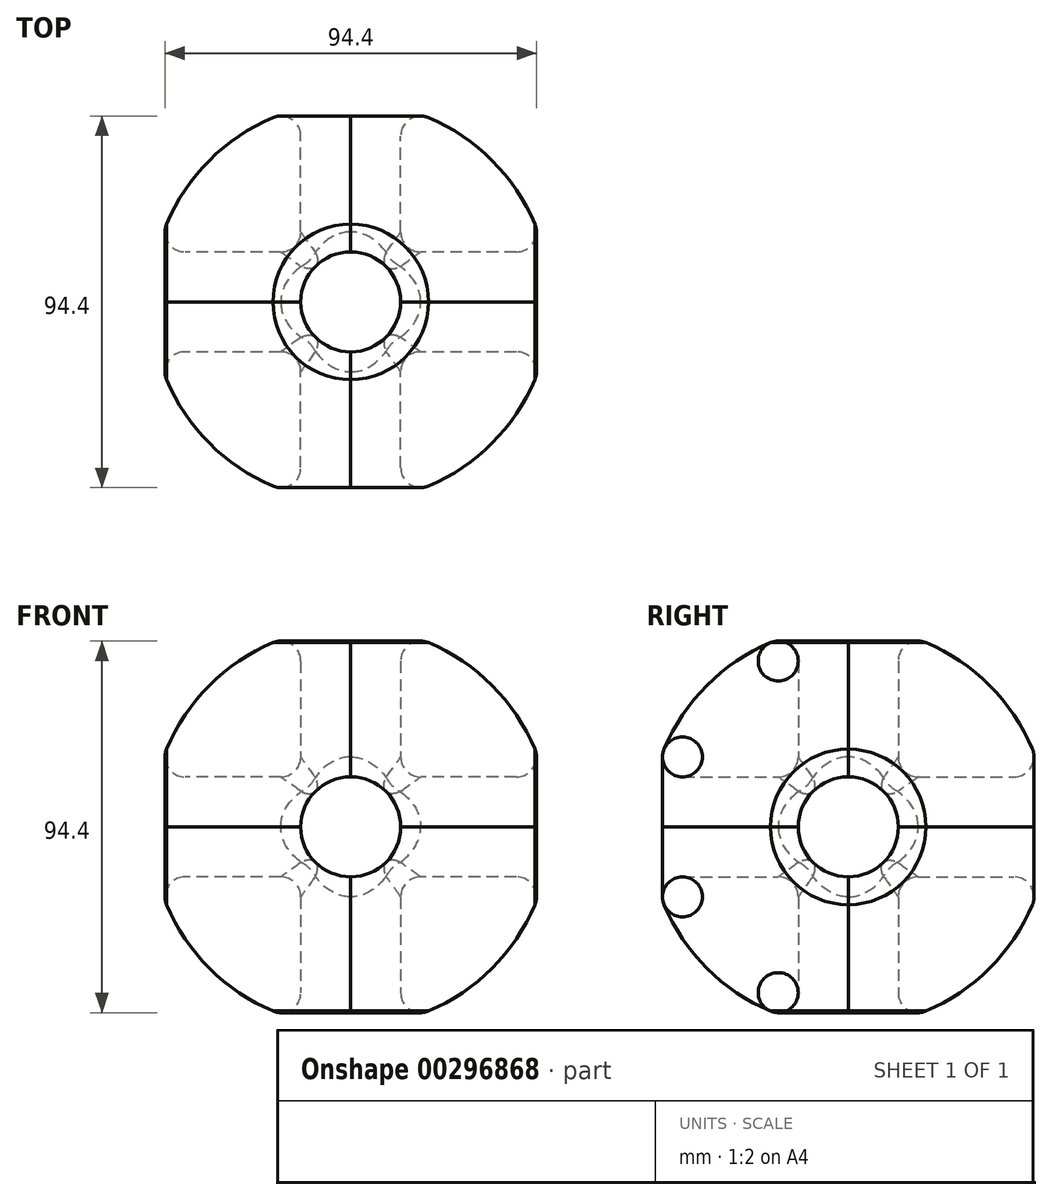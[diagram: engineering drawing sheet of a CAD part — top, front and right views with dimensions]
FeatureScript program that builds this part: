
annotation { "Feature Type Name" : "Feature", "Feature Type Description" : "" }
export const myFeature = defineFeature(function(context is Context, id is Id, definition is map)
    precondition{}
    {
        {
            var Q0;
            Q0=qCreatedBy(makeId("Top.planeOp"),FACE);
            var sketch = newSketch(context, id + "F0", { "sketchPlane" : qUnion([Q0])});
            skCircle(sketch, "E0", {"center": v(0, 0) * mm, "radius": 50.8 * mm});
            skLineSegment(sketch, "E1", {"start": v(0, 50.8) * mm, "end": v(0, -50.8) * mm});
            skLineSegment(sketch, "E2", {"start": v(-50.8, 0) * mm, "end": v(50.8, 0) * mm});
            skSolve(sketch);
        }
        {
            var Q0;
            Q0=qCreatedBy(makeId("Top.planeOp"),FACE);
            var sketch = newSketch(context, id + "F1", { "sketchPlane" : qUnion([Q0])});
            skCircle(sketch, "E3", {"center": v(0, 0) * mm, "radius": 12.7 * mm});
            skSolve(sketch);
        }
        {
            var Q0;
            Q0=qCreatedBy(makeId("Right.planeOp"),FACE);
            var sketch = newSketch(context, id + "F2", { "sketchPlane" : qUnion([Q0])});
            skCircle(sketch, "E4", {"center": v(0, 0) * mm, "radius": 12.7 * mm});
            skSolve(sketch);
        }
        {
            var Q0;
            Q0=qCreatedBy(makeId("Front.planeOp"),FACE);
            var sketch = newSketch(context, id + "F3", { "sketchPlane" : qUnion([Q0])});
            skCircle(sketch, "E5", {"center": v(0, 0) * mm, "radius": 12.7 * mm});
            skSolve(sketch);
        }
        {
            var Q0;
            {var subQ0=sQuery(id+"F0.wireOp",EDGE,"E1");var subQ1=sQuery(id+"F0.wireOp",EDGE,"E0");var subQ2=makeQuery(id+"F0.imprint","INTERSECT",VERTEX,{"disambiguationData":[OD(0.0)],"derivedFrom":[subQ1,subQ0]});Q0=makeQuery(id+"F0.imprint","IMPRINT",FACE,{"disambiguationData":[TD([[makeQuery(id+"F0.imprint","IMPRINT",EDGE,{"disambiguationData":[TD([[subQ2,-1.0]])],"derivedFrom":subQ1}),1.0]])]});}
            var Q1;
            Q1=sQuery(id+"F0.wireOp",EDGE,"E1");
            revolve(context, id + "F4", {"entities" : qUnion([Q0]), "axis" : qUnion([Q1]), "revolveType" : RevolveType.ONE_DIRECTION, "oppositeDirection" : true, "angle" : 90 * degree});
        }
        {
            var Q0;
            {var subQ0=sQuery(id+"F0.wireOp",EDGE,"E1");var subQ1=sQuery(id+"F0.wireOp",EDGE,"E0");var subQ2=makeQuery(id+"F0.imprint","INTERSECT",VERTEX,{"disambiguationData":[OD(0.0)],"derivedFrom":[subQ1,subQ0]});Q0=makeQuery(id+"F0.imprint","IMPRINT",FACE,{"disambiguationData":[TD([[makeQuery(id+"F0.imprint","IMPRINT",EDGE,{"disambiguationData":[TD([[subQ2,1.0]])],"derivedFrom":subQ1}),1.0]])]});}
            var Q1;
            Q1=sQuery(id+"F0.wireOp",EDGE,"E1");
            revolve(context, id + "F5", {"entities" : qUnion([Q0]), "axis" : qUnion([Q1]), "revolveType" : RevolveType.ONE_DIRECTION, "angle" : 90 * degree});
        }
        {
            var Q0;
            {var subQ0=sQuery(id+"F0.wireOp",EDGE,"E1");var subQ1=sQuery(id+"F0.wireOp",EDGE,"E0");var subQ2=makeQuery(id+"F0.imprint","INTERSECT",VERTEX,{"disambiguationData":[OD(1.0)],"derivedFrom":[subQ1,subQ0]});Q0=makeQuery(id+"F0.imprint","IMPRINT",FACE,{"disambiguationData":[TD([[makeQuery(id+"F0.imprint","IMPRINT",EDGE,{"disambiguationData":[TD([[subQ2,1.0]])],"derivedFrom":subQ1}),1.0]])]});}
            var Q1;
            Q1=sQuery(id+"F0.wireOp",EDGE,"E1");
            revolve(context, id + "F6", {"entities" : qUnion([Q0]), "axis" : qUnion([Q1]), "revolveType" : RevolveType.ONE_DIRECTION, "oppositeDirection" : true, "angle" : 90 * degree});
        }
        {
            var Q0;
            {var subQ0=sQuery(id+"F0.wireOp",EDGE,"E1");var subQ1=sQuery(id+"F0.wireOp",EDGE,"E0");var subQ2=makeQuery(id+"F0.imprint","INTERSECT",VERTEX,{"disambiguationData":[OD(1.0)],"derivedFrom":[subQ1,subQ0]});Q0=makeQuery(id+"F0.imprint","IMPRINT",FACE,{"disambiguationData":[TD([[makeQuery(id+"F0.imprint","IMPRINT",EDGE,{"disambiguationData":[TD([[subQ2,-1.0]])],"derivedFrom":subQ1}),1.0]])]});}
            var Q1;
            Q1=sQuery(id+"F0.wireOp",EDGE,"E1");
            revolve(context, id + "F7", {"entities" : qUnion([Q0]), "axis" : qUnion([Q1]), "revolveType" : RevolveType.ONE_DIRECTION, "angle" : 90 * degree});
        }
        {
            var Q0;
            {var subQ0=sQuery(id+"F0.wireOp",EDGE,"E1");var subQ1=sQuery(id+"F0.wireOp",EDGE,"E0");var subQ2=makeQuery(id+"F0.imprint","INTERSECT",VERTEX,{"disambiguationData":[OD(1.0)],"derivedFrom":[subQ1,subQ0]});Q0=makeQuery(id+"F0.imprint","IMPRINT",FACE,{"disambiguationData":[TD([[makeQuery(id+"F0.imprint","IMPRINT",EDGE,{"disambiguationData":[TD([[subQ2,1.0]])],"derivedFrom":subQ1}),1.0]])]});}
            var Q1;
            Q1=sQuery(id+"F0.wireOp",EDGE,"E1");
            revolve(context, id + "F8", {"entities" : qUnion([Q0]), "axis" : qUnion([Q1]), "revolveType" : RevolveType.ONE_DIRECTION, "angle" : 90 * degree});
        }
        {
            var Q0;
            {var subQ0=sQuery(id+"F0.wireOp",EDGE,"E1");var subQ1=sQuery(id+"F0.wireOp",EDGE,"E0");var subQ2=makeQuery(id+"F0.imprint","INTERSECT",VERTEX,{"disambiguationData":[OD(1.0)],"derivedFrom":[subQ1,subQ0]});Q0=makeQuery(id+"F0.imprint","IMPRINT",FACE,{"disambiguationData":[TD([[makeQuery(id+"F0.imprint","IMPRINT",EDGE,{"disambiguationData":[TD([[subQ2,-1.0]])],"derivedFrom":subQ1}),1.0]])]});}
            var Q1;
            Q1=sQuery(id+"F0.wireOp",EDGE,"E1");
            revolve(context, id + "F9", {"entities" : qUnion([Q0]), "axis" : qUnion([Q1]), "revolveType" : RevolveType.ONE_DIRECTION, "oppositeDirection" : true, "angle" : 90 * degree});
        }
        {
            var Q0;
            {var subQ0=sQuery(id+"F0.wireOp",EDGE,"E1");var subQ1=sQuery(id+"F0.wireOp",EDGE,"E0");var subQ2=makeQuery(id+"F0.imprint","INTERSECT",VERTEX,{"disambiguationData":[OD(0.0)],"derivedFrom":[subQ1,subQ0]});Q0=makeQuery(id+"F0.imprint","IMPRINT",FACE,{"disambiguationData":[TD([[makeQuery(id+"F0.imprint","IMPRINT",EDGE,{"disambiguationData":[TD([[subQ2,-1.0]])],"derivedFrom":subQ1}),1.0]])]});}
            var Q1;
            Q1=sQuery(id+"F0.wireOp",EDGE,"E1");
            revolve(context, id + "F10", {"entities" : qUnion([Q0]), "axis" : qUnion([Q1]), "revolveType" : RevolveType.ONE_DIRECTION, "angle" : 90 * degree});
        }
        {
            var Q0;
            {var subQ0=sQuery(id+"F0.wireOp",EDGE,"E1");var subQ1=sQuery(id+"F0.wireOp",EDGE,"E0");var subQ2=makeQuery(id+"F0.imprint","INTERSECT",VERTEX,{"disambiguationData":[OD(0.0)],"derivedFrom":[subQ1,subQ0]});Q0=makeQuery(id+"F0.imprint","IMPRINT",FACE,{"disambiguationData":[TD([[makeQuery(id+"F0.imprint","IMPRINT",EDGE,{"disambiguationData":[TD([[subQ2,1.0]])],"derivedFrom":subQ1}),1.0]])]});}
            var Q1;
            Q1=sQuery(id+"F0.wireOp",EDGE,"E1");
            revolve(context, id + "F11", {"entities" : qUnion([Q0]), "axis" : qUnion([Q1]), "revolveType" : RevolveType.ONE_DIRECTION, "oppositeDirection" : true, "angle" : 90 * degree});
        }
        {
            var Q0;
            Q0 = qSketchRegion(id + "F1", true);
            extrude(context, id + "F12", {"entities" : qUnion([Q0]), "operationType" : NewBodyOperationType.REMOVE, "endBound" : BoundingType.SYMMETRIC, "depth" : 101.6 * mm});
        }
        {
            var Q0;
            Q0 = qSketchRegion(id + "F2", true);
            extrude(context, id + "F13", {"entities" : qUnion([Q0]), "operationType" : NewBodyOperationType.REMOVE, "endBound" : BoundingType.SYMMETRIC, "depth" : 101.6 * mm});
        }
        {
            var Q0;
            Q0 = qSketchRegion(id + "F3", true);
            extrude(context, id + "F14", {"entities" : qUnion([Q0]), "operationType" : NewBodyOperationType.REMOVE, "endBound" : BoundingType.SYMMETRIC, "depth" : 101.6 * mm});
        }
        {
            var Q0;
            Q0=makeQuery(id+"F13.boolean.opBoolean","INTERSECT",EDGE,{"derivedFrom":[makeQuery(id+"F5.opRevolve","SWEPT_FACE",FACE,{"disambiguationData":[OSD([sQuery(id+"F0.wireOp",EDGE,"E0")])]}),makeQuery(id+"F13.opExtrude","SWEPT_FACE",FACE,{"disambiguationData":[OSD([sQuery(id+"F2.wireOp",EDGE,"E4")])]})]});
            var Q1;
            Q1=makeQuery(id+"F13.boolean.opBoolean","INTERSECT",EDGE,{"derivedFrom":[makeQuery(id+"F7.opRevolve","SWEPT_FACE",FACE,{"disambiguationData":[OSD([sQuery(id+"F0.wireOp",EDGE,"E0")])]}),makeQuery(id+"F13.opExtrude","SWEPT_FACE",FACE,{"disambiguationData":[OSD([sQuery(id+"F2.wireOp",EDGE,"E4")])]})]});
            var Q2;
            Q2=makeQuery(id+"F13.boolean.opBoolean","INTERSECT",EDGE,{"derivedFrom":[makeQuery(id+"F9.opRevolve","SWEPT_FACE",FACE,{"disambiguationData":[OSD([sQuery(id+"F0.wireOp",EDGE,"E0")])]}),makeQuery(id+"F13.opExtrude","SWEPT_FACE",FACE,{"disambiguationData":[OSD([sQuery(id+"F2.wireOp",EDGE,"E4")])]})]});
            var Q3;
            Q3=makeQuery(id+"F13.boolean.opBoolean","INTERSECT",EDGE,{"derivedFrom":[makeQuery(id+"F11.opRevolve","SWEPT_FACE",FACE,{"disambiguationData":[OSD([sQuery(id+"F0.wireOp",EDGE,"E0")])]}),makeQuery(id+"F13.opExtrude","SWEPT_FACE",FACE,{"disambiguationData":[OSD([sQuery(id+"F2.wireOp",EDGE,"E4")])]})]});
            var Q4;
            Q4=makeQuery(id+"F12.boolean.opBoolean","INTERSECT",EDGE,{"derivedFrom":[makeQuery(id+"F7.opRevolve","SWEPT_FACE",FACE,{"disambiguationData":[OSD([sQuery(id+"F0.wireOp",EDGE,"E0")])]}),makeQuery(id+"F12.opExtrude","SWEPT_FACE",FACE,{"disambiguationData":[OSD([sQuery(id+"F1.wireOp",EDGE,"E3")])]})]});
            var Q5;
            Q5=makeQuery(id+"F12.boolean.opBoolean","INTERSECT",EDGE,{"derivedFrom":[makeQuery(id+"F5.opRevolve","SWEPT_FACE",FACE,{"disambiguationData":[OSD([sQuery(id+"F0.wireOp",EDGE,"E0")])]}),makeQuery(id+"F12.opExtrude","SWEPT_FACE",FACE,{"disambiguationData":[OSD([sQuery(id+"F1.wireOp",EDGE,"E3")])]})]});
            var Q6;
            Q6=makeQuery(id+"F12.boolean.opBoolean","INTERSECT",EDGE,{"derivedFrom":[makeQuery(id+"F6.opRevolve","SWEPT_FACE",FACE,{"disambiguationData":[OSD([sQuery(id+"F0.wireOp",EDGE,"E0")])]}),makeQuery(id+"F12.opExtrude","SWEPT_FACE",FACE,{"disambiguationData":[OSD([sQuery(id+"F1.wireOp",EDGE,"E3")])]})]});
            var Q7;
            Q7=makeQuery(id+"F12.boolean.opBoolean","INTERSECT",EDGE,{"derivedFrom":[makeQuery(id+"F4.opRevolve","SWEPT_FACE",FACE,{"disambiguationData":[OSD([sQuery(id+"F0.wireOp",EDGE,"E0")])]}),makeQuery(id+"F12.opExtrude","SWEPT_FACE",FACE,{"disambiguationData":[OSD([sQuery(id+"F1.wireOp",EDGE,"E3")])]})]});
            var Q8;
            Q8=makeQuery(id+"F14.boolean.opBoolean","INTERSECT",EDGE,{"derivedFrom":[makeQuery(id+"F5.opRevolve","SWEPT_FACE",FACE,{"disambiguationData":[OSD([sQuery(id+"F0.wireOp",EDGE,"E0")])]}),makeQuery(id+"F14.opExtrude","SWEPT_FACE",FACE,{"disambiguationData":[OSD([sQuery(id+"F3.wireOp",EDGE,"E5")])]})]});
            var Q9;
            Q9=makeQuery(id+"F14.boolean.opBoolean","INTERSECT",EDGE,{"derivedFrom":[makeQuery(id+"F11.opRevolve","SWEPT_FACE",FACE,{"disambiguationData":[OSD([sQuery(id+"F0.wireOp",EDGE,"E0")])]}),makeQuery(id+"F14.opExtrude","SWEPT_FACE",FACE,{"disambiguationData":[OSD([sQuery(id+"F3.wireOp",EDGE,"E5")])]})]});
            var Q10;
            Q10=makeQuery(id+"F14.boolean.opBoolean","INTERSECT",EDGE,{"derivedFrom":[makeQuery(id+"F4.opRevolve","SWEPT_FACE",FACE,{"disambiguationData":[OSD([sQuery(id+"F0.wireOp",EDGE,"E0")])]}),makeQuery(id+"F14.opExtrude","SWEPT_FACE",FACE,{"disambiguationData":[OSD([sQuery(id+"F3.wireOp",EDGE,"E5")])]})]});
            var Q11;
            Q11=makeQuery(id+"F14.boolean.opBoolean","INTERSECT",EDGE,{"derivedFrom":[makeQuery(id+"F10.opRevolve","SWEPT_FACE",FACE,{"disambiguationData":[OSD([sQuery(id+"F0.wireOp",EDGE,"E0")])]}),makeQuery(id+"F14.opExtrude","SWEPT_FACE",FACE,{"disambiguationData":[OSD([sQuery(id+"F3.wireOp",EDGE,"E5")])]})]});
            var Q12;
            Q12=makeQuery(id+"F13.boolean.opBoolean","INTERSECT",EDGE,{"derivedFrom":[makeQuery(id+"F6.opRevolve","SWEPT_FACE",FACE,{"disambiguationData":[OSD([sQuery(id+"F0.wireOp",EDGE,"E0")])]}),makeQuery(id+"F13.opExtrude","SWEPT_FACE",FACE,{"disambiguationData":[OSD([sQuery(id+"F2.wireOp",EDGE,"E4")])]})]});
            var Q13;
            Q13=makeQuery(id+"F13.boolean.opBoolean","INTERSECT",EDGE,{"derivedFrom":[makeQuery(id+"F4.opRevolve","SWEPT_FACE",FACE,{"disambiguationData":[OSD([sQuery(id+"F0.wireOp",EDGE,"E0")])]}),makeQuery(id+"F13.opExtrude","SWEPT_FACE",FACE,{"disambiguationData":[OSD([sQuery(id+"F2.wireOp",EDGE,"E4")])]})]});
            var Q14;
            Q14=makeQuery(id+"F13.boolean.opBoolean","INTERSECT",EDGE,{"derivedFrom":[makeQuery(id+"F8.opRevolve","SWEPT_FACE",FACE,{"disambiguationData":[OSD([sQuery(id+"F0.wireOp",EDGE,"E0")])]}),makeQuery(id+"F13.opExtrude","SWEPT_FACE",FACE,{"disambiguationData":[OSD([sQuery(id+"F2.wireOp",EDGE,"E4")])]})]});
            var Q15;
            Q15=makeQuery(id+"F13.boolean.opBoolean","INTERSECT",EDGE,{"derivedFrom":[makeQuery(id+"F10.opRevolve","SWEPT_FACE",FACE,{"disambiguationData":[OSD([sQuery(id+"F0.wireOp",EDGE,"E0")])]}),makeQuery(id+"F13.opExtrude","SWEPT_FACE",FACE,{"disambiguationData":[OSD([sQuery(id+"F2.wireOp",EDGE,"E4")])]})]});
            var Q16;
            Q16=makeQuery(id+"F14.boolean.opBoolean","INTERSECT",EDGE,{"derivedFrom":[makeQuery(id+"F6.opRevolve","SWEPT_FACE",FACE,{"disambiguationData":[OSD([sQuery(id+"F0.wireOp",EDGE,"E0")])]}),makeQuery(id+"F14.opExtrude","SWEPT_FACE",FACE,{"disambiguationData":[OSD([sQuery(id+"F3.wireOp",EDGE,"E5")])]})]});
            var Q17;
            Q17=makeQuery(id+"F14.boolean.opBoolean","INTERSECT",EDGE,{"derivedFrom":[makeQuery(id+"F8.opRevolve","SWEPT_FACE",FACE,{"disambiguationData":[OSD([sQuery(id+"F0.wireOp",EDGE,"E0")])]}),makeQuery(id+"F14.opExtrude","SWEPT_FACE",FACE,{"disambiguationData":[OSD([sQuery(id+"F3.wireOp",EDGE,"E5")])]})]});
            var Q18;
            Q18=makeQuery(id+"F14.boolean.opBoolean","INTERSECT",EDGE,{"derivedFrom":[makeQuery(id+"F7.opRevolve","SWEPT_FACE",FACE,{"disambiguationData":[OSD([sQuery(id+"F0.wireOp",EDGE,"E0")])]}),makeQuery(id+"F14.opExtrude","SWEPT_FACE",FACE,{"disambiguationData":[OSD([sQuery(id+"F3.wireOp",EDGE,"E5")])]})]});
            var Q19;
            Q19=makeQuery(id+"F14.boolean.opBoolean","INTERSECT",EDGE,{"derivedFrom":[makeQuery(id+"F9.opRevolve","SWEPT_FACE",FACE,{"disambiguationData":[OSD([sQuery(id+"F0.wireOp",EDGE,"E0")])]}),makeQuery(id+"F14.opExtrude","SWEPT_FACE",FACE,{"disambiguationData":[OSD([sQuery(id+"F3.wireOp",EDGE,"E5")])]})]});
            var Q20;
            Q20=makeQuery(id+"F12.boolean.opBoolean","INTERSECT",EDGE,{"derivedFrom":[makeQuery(id+"F8.opRevolve","SWEPT_FACE",FACE,{"disambiguationData":[OSD([sQuery(id+"F0.wireOp",EDGE,"E0")])]}),makeQuery(id+"F12.opExtrude","SWEPT_FACE",FACE,{"disambiguationData":[OSD([sQuery(id+"F1.wireOp",EDGE,"E3")])]})]});
            var Q21;
            Q21=makeQuery(id+"F12.boolean.opBoolean","INTERSECT",EDGE,{"derivedFrom":[makeQuery(id+"F10.opRevolve","SWEPT_FACE",FACE,{"disambiguationData":[OSD([sQuery(id+"F0.wireOp",EDGE,"E0")])]}),makeQuery(id+"F12.opExtrude","SWEPT_FACE",FACE,{"disambiguationData":[OSD([sQuery(id+"F1.wireOp",EDGE,"E3")])]})]});
            var Q22;
            Q22=makeQuery(id+"F12.boolean.opBoolean","INTERSECT",EDGE,{"derivedFrom":[makeQuery(id+"F9.opRevolve","SWEPT_FACE",FACE,{"disambiguationData":[OSD([sQuery(id+"F0.wireOp",EDGE,"E0")])]}),makeQuery(id+"F12.opExtrude","SWEPT_FACE",FACE,{"disambiguationData":[OSD([sQuery(id+"F1.wireOp",EDGE,"E3")])]})]});
            var Q23;
            Q23=makeQuery(id+"F12.boolean.opBoolean","INTERSECT",EDGE,{"derivedFrom":[makeQuery(id+"F11.opRevolve","SWEPT_FACE",FACE,{"disambiguationData":[OSD([sQuery(id+"F0.wireOp",EDGE,"E0")])]}),makeQuery(id+"F12.opExtrude","SWEPT_FACE",FACE,{"disambiguationData":[OSD([sQuery(id+"F1.wireOp",EDGE,"E3")])]})]});
            fillet(context, id + "F15", {"entities" : qUnion([Q0, Q1, Q2, Q3, Q4, Q5, Q6, Q7, Q8, Q9, Q10, Q11, Q12, Q13, Q14, Q15, Q16, Q17, Q18, Q19, Q20, Q21, Q22, Q23]), "radius" : 5.08 * mm, "tangentPropagation" : true, "allowEdgeOverflow" : false});
        }
        {
            var Q0;
            {var subQ0=sQuery(id+"F0.wireOp",EDGE,"E0");Q0=makeQuery(id+"F13.boolean.opBoolean","INTERSECT",EDGE,{"derivedFrom":[makeQuery(id+"F12.boolean.opBoolean","COPY",FACE,{"disambiguationData":[TD([makeQuery(id+"F6.opRevolve","SWEPT_FACE",FACE,{"disambiguationData":[OSD([subQ0])]})])],"derivedFrom":makeQuery(id+"F12.opExtrude","SWEPT_FACE",FACE,{"disambiguationData":[OSD([sQuery(id+"F1.wireOp",EDGE,"E3")])]})}),makeQuery(id+"F13.opExtrude","SWEPT_FACE",FACE,{"disambiguationData":[OSD([sQuery(id+"F2.wireOp",EDGE,"E4")])]})]});}
            var Q1;
            {var subQ0=sQuery(id+"F0.wireOp",EDGE,"E0");Q1=makeQuery(id+"F13.boolean.opBoolean","INTERSECT",EDGE,{"derivedFrom":[makeQuery(id+"F12.boolean.opBoolean","COPY",FACE,{"disambiguationData":[TD([makeQuery(id+"F4.opRevolve","SWEPT_FACE",FACE,{"disambiguationData":[OSD([subQ0])]})])],"derivedFrom":makeQuery(id+"F12.opExtrude","SWEPT_FACE",FACE,{"disambiguationData":[OSD([sQuery(id+"F1.wireOp",EDGE,"E3")])]})}),makeQuery(id+"F13.opExtrude","SWEPT_FACE",FACE,{"disambiguationData":[OSD([sQuery(id+"F2.wireOp",EDGE,"E4")])]})]});}
            var Q2;
            {var subQ0=sQuery(id+"F0.wireOp",EDGE,"E0");Q2=makeQuery(id+"F13.boolean.opBoolean","INTERSECT",EDGE,{"derivedFrom":[makeQuery(id+"F12.boolean.opBoolean","COPY",FACE,{"disambiguationData":[TD([makeQuery(id+"F8.opRevolve","SWEPT_FACE",FACE,{"disambiguationData":[OSD([subQ0])]})])],"derivedFrom":makeQuery(id+"F12.opExtrude","SWEPT_FACE",FACE,{"disambiguationData":[OSD([sQuery(id+"F1.wireOp",EDGE,"E3")])]})}),makeQuery(id+"F13.opExtrude","SWEPT_FACE",FACE,{"disambiguationData":[OSD([sQuery(id+"F2.wireOp",EDGE,"E4")])]})]});}
            var Q3;
            {var subQ0=sQuery(id+"F0.wireOp",EDGE,"E0");Q3=makeQuery(id+"F13.boolean.opBoolean","INTERSECT",EDGE,{"derivedFrom":[makeQuery(id+"F12.boolean.opBoolean","COPY",FACE,{"disambiguationData":[TD([makeQuery(id+"F10.opRevolve","SWEPT_FACE",FACE,{"disambiguationData":[OSD([subQ0])]})])],"derivedFrom":makeQuery(id+"F12.opExtrude","SWEPT_FACE",FACE,{"disambiguationData":[OSD([sQuery(id+"F1.wireOp",EDGE,"E3")])]})}),makeQuery(id+"F13.opExtrude","SWEPT_FACE",FACE,{"disambiguationData":[OSD([sQuery(id+"F2.wireOp",EDGE,"E4")])]})]});}
            var Q4;
            {var subQ3=sQuery(id+"F0.wireOp",EDGE,"E0");var subQ5=makeQuery(id+"F4.opRevolve","SWEPT_FACE",FACE,{"disambiguationData":[OSD([subQ3])]});Q4=makeQuery(id+"F14.boolean.opBoolean","INTERSECT",EDGE,{"derivedFrom":[makeQuery(id+"F13.boolean.opBoolean","COPY",FACE,{"disambiguationData":[TD([subQ5])],"derivedFrom":makeQuery(id+"F13.opExtrude","SWEPT_FACE",FACE,{"disambiguationData":[OSD([sQuery(id+"F2.wireOp",EDGE,"E4")])]})}),makeQuery(id+"F14.opExtrude","SWEPT_FACE",FACE,{"disambiguationData":[OSD([sQuery(id+"F3.wireOp",EDGE,"E5")])]})]});}
            var Q5;
            {var subQ3=sQuery(id+"F0.wireOp",EDGE,"E0");var subQ6=makeQuery(id+"F10.opRevolve","SWEPT_FACE",FACE,{"disambiguationData":[OSD([subQ3])]});Q5=makeQuery(id+"F14.boolean.opBoolean","INTERSECT",EDGE,{"derivedFrom":[makeQuery(id+"F13.boolean.opBoolean","COPY",FACE,{"disambiguationData":[TD([subQ6])],"derivedFrom":makeQuery(id+"F13.opExtrude","SWEPT_FACE",FACE,{"disambiguationData":[OSD([sQuery(id+"F2.wireOp",EDGE,"E4")])]})}),makeQuery(id+"F14.opExtrude","SWEPT_FACE",FACE,{"disambiguationData":[OSD([sQuery(id+"F3.wireOp",EDGE,"E5")])]})]});}
            var Q6;
            {var subQ3=sQuery(id+"F0.wireOp",EDGE,"E0");var subQ6=makeQuery(id+"F6.opRevolve","SWEPT_FACE",FACE,{"disambiguationData":[OSD([subQ3])]});Q6=makeQuery(id+"F14.boolean.opBoolean","INTERSECT",EDGE,{"derivedFrom":[makeQuery(id+"F13.boolean.opBoolean","COPY",FACE,{"disambiguationData":[TD([subQ6])],"derivedFrom":makeQuery(id+"F13.opExtrude","SWEPT_FACE",FACE,{"disambiguationData":[OSD([sQuery(id+"F2.wireOp",EDGE,"E4")])]})}),makeQuery(id+"F14.opExtrude","SWEPT_FACE",FACE,{"disambiguationData":[OSD([sQuery(id+"F3.wireOp",EDGE,"E5")])]})]});}
            var Q7;
            {var subQ3=sQuery(id+"F0.wireOp",EDGE,"E0");var subQ6=makeQuery(id+"F8.opRevolve","SWEPT_FACE",FACE,{"disambiguationData":[OSD([subQ3])]});Q7=makeQuery(id+"F14.boolean.opBoolean","INTERSECT",EDGE,{"derivedFrom":[makeQuery(id+"F13.boolean.opBoolean","COPY",FACE,{"disambiguationData":[TD([subQ6])],"derivedFrom":makeQuery(id+"F13.opExtrude","SWEPT_FACE",FACE,{"disambiguationData":[OSD([sQuery(id+"F2.wireOp",EDGE,"E4")])]})}),makeQuery(id+"F14.opExtrude","SWEPT_FACE",FACE,{"disambiguationData":[OSD([sQuery(id+"F3.wireOp",EDGE,"E5")])]})]});}
            var Q8;
            {var subQ0=sQuery(id+"F0.wireOp",EDGE,"E0");Q8=makeQuery(id+"F13.boolean.opBoolean","INTERSECT",EDGE,{"derivedFrom":[makeQuery(id+"F12.boolean.opBoolean","COPY",FACE,{"disambiguationData":[TD([makeQuery(id+"F5.opRevolve","SWEPT_FACE",FACE,{"disambiguationData":[OSD([subQ0])]})])],"derivedFrom":makeQuery(id+"F12.opExtrude","SWEPT_FACE",FACE,{"disambiguationData":[OSD([sQuery(id+"F1.wireOp",EDGE,"E3")])]})}),makeQuery(id+"F13.opExtrude","SWEPT_FACE",FACE,{"disambiguationData":[OSD([sQuery(id+"F2.wireOp",EDGE,"E4")])]})]});}
            var Q9;
            {var subQ0=sQuery(id+"F0.wireOp",EDGE,"E0");Q9=makeQuery(id+"F13.boolean.opBoolean","INTERSECT",EDGE,{"derivedFrom":[makeQuery(id+"F12.boolean.opBoolean","COPY",FACE,{"disambiguationData":[TD([makeQuery(id+"F7.opRevolve","SWEPT_FACE",FACE,{"disambiguationData":[OSD([subQ0])]})])],"derivedFrom":makeQuery(id+"F12.opExtrude","SWEPT_FACE",FACE,{"disambiguationData":[OSD([sQuery(id+"F1.wireOp",EDGE,"E3")])]})}),makeQuery(id+"F13.opExtrude","SWEPT_FACE",FACE,{"disambiguationData":[OSD([sQuery(id+"F2.wireOp",EDGE,"E4")])]})]});}
            var Q10;
            {var subQ0=sQuery(id+"F0.wireOp",EDGE,"E0");Q10=makeQuery(id+"F14.boolean.opBoolean","INTERSECT",EDGE,{"derivedFrom":[makeQuery(id+"F12.boolean.opBoolean","COPY",FACE,{"disambiguationData":[TD([makeQuery(id+"F4.opRevolve","SWEPT_FACE",FACE,{"disambiguationData":[OSD([subQ0])]})])],"derivedFrom":makeQuery(id+"F12.opExtrude","SWEPT_FACE",FACE,{"disambiguationData":[OSD([sQuery(id+"F1.wireOp",EDGE,"E3")])]})}),makeQuery(id+"F14.opExtrude","SWEPT_FACE",FACE,{"disambiguationData":[OSD([sQuery(id+"F3.wireOp",EDGE,"E5")])]})]});}
            var Q11;
            {var subQ0=sQuery(id+"F0.wireOp",EDGE,"E0");Q11=makeQuery(id+"F14.boolean.opBoolean","INTERSECT",EDGE,{"derivedFrom":[makeQuery(id+"F12.boolean.opBoolean","COPY",FACE,{"disambiguationData":[TD([makeQuery(id+"F5.opRevolve","SWEPT_FACE",FACE,{"disambiguationData":[OSD([subQ0])]})])],"derivedFrom":makeQuery(id+"F12.opExtrude","SWEPT_FACE",FACE,{"disambiguationData":[OSD([sQuery(id+"F1.wireOp",EDGE,"E3")])]})}),makeQuery(id+"F14.opExtrude","SWEPT_FACE",FACE,{"disambiguationData":[OSD([sQuery(id+"F3.wireOp",EDGE,"E5")])]})]});}
            var Q12;
            {var subQ0=sQuery(id+"F0.wireOp",EDGE,"E0");Q12=makeQuery(id+"F14.boolean.opBoolean","INTERSECT",EDGE,{"derivedFrom":[makeQuery(id+"F12.boolean.opBoolean","COPY",FACE,{"disambiguationData":[TD([makeQuery(id+"F7.opRevolve","SWEPT_FACE",FACE,{"disambiguationData":[OSD([subQ0])]})])],"derivedFrom":makeQuery(id+"F12.opExtrude","SWEPT_FACE",FACE,{"disambiguationData":[OSD([sQuery(id+"F1.wireOp",EDGE,"E3")])]})}),makeQuery(id+"F14.opExtrude","SWEPT_FACE",FACE,{"disambiguationData":[OSD([sQuery(id+"F3.wireOp",EDGE,"E5")])]})]});}
            var Q13;
            {var subQ0=sQuery(id+"F0.wireOp",EDGE,"E0");Q13=makeQuery(id+"F14.boolean.opBoolean","INTERSECT",EDGE,{"derivedFrom":[makeQuery(id+"F12.boolean.opBoolean","COPY",FACE,{"disambiguationData":[TD([makeQuery(id+"F6.opRevolve","SWEPT_FACE",FACE,{"disambiguationData":[OSD([subQ0])]})])],"derivedFrom":makeQuery(id+"F12.opExtrude","SWEPT_FACE",FACE,{"disambiguationData":[OSD([sQuery(id+"F1.wireOp",EDGE,"E3")])]})}),makeQuery(id+"F14.opExtrude","SWEPT_FACE",FACE,{"disambiguationData":[OSD([sQuery(id+"F3.wireOp",EDGE,"E5")])]})]});}
            var Q14;
            {var subQ0=sQuery(id+"F0.wireOp",EDGE,"E0");Q14=makeQuery(id+"F14.boolean.opBoolean","INTERSECT",EDGE,{"derivedFrom":[makeQuery(id+"F12.boolean.opBoolean","COPY",FACE,{"disambiguationData":[TD([makeQuery(id+"F9.opRevolve","SWEPT_FACE",FACE,{"disambiguationData":[OSD([subQ0])]})])],"derivedFrom":makeQuery(id+"F12.opExtrude","SWEPT_FACE",FACE,{"disambiguationData":[OSD([sQuery(id+"F1.wireOp",EDGE,"E3")])]})}),makeQuery(id+"F14.opExtrude","SWEPT_FACE",FACE,{"disambiguationData":[OSD([sQuery(id+"F3.wireOp",EDGE,"E5")])]})]});}
            var Q15;
            {var subQ3=sQuery(id+"F0.wireOp",EDGE,"E0");var subQ6=makeQuery(id+"F7.opRevolve","SWEPT_FACE",FACE,{"disambiguationData":[OSD([subQ3])]});Q15=makeQuery(id+"F14.boolean.opBoolean","INTERSECT",EDGE,{"derivedFrom":[makeQuery(id+"F13.boolean.opBoolean","COPY",FACE,{"disambiguationData":[TD([subQ6])],"derivedFrom":makeQuery(id+"F13.opExtrude","SWEPT_FACE",FACE,{"disambiguationData":[OSD([sQuery(id+"F2.wireOp",EDGE,"E4")])]})}),makeQuery(id+"F14.opExtrude","SWEPT_FACE",FACE,{"disambiguationData":[OSD([sQuery(id+"F3.wireOp",EDGE,"E5")])]})]});}
            var Q16;
            {var subQ3=sQuery(id+"F0.wireOp",EDGE,"E0");var subQ6=makeQuery(id+"F9.opRevolve","SWEPT_FACE",FACE,{"disambiguationData":[OSD([subQ3])]});Q16=makeQuery(id+"F14.boolean.opBoolean","INTERSECT",EDGE,{"derivedFrom":[makeQuery(id+"F13.boolean.opBoolean","COPY",FACE,{"disambiguationData":[TD([subQ6])],"derivedFrom":makeQuery(id+"F13.opExtrude","SWEPT_FACE",FACE,{"disambiguationData":[OSD([sQuery(id+"F2.wireOp",EDGE,"E4")])]})}),makeQuery(id+"F14.opExtrude","SWEPT_FACE",FACE,{"disambiguationData":[OSD([sQuery(id+"F3.wireOp",EDGE,"E5")])]})]});}
            var Q17;
            {var subQ3=sQuery(id+"F0.wireOp",EDGE,"E0");var subQ6=makeQuery(id+"F5.opRevolve","SWEPT_FACE",FACE,{"disambiguationData":[OSD([subQ3])]});Q17=makeQuery(id+"F14.boolean.opBoolean","INTERSECT",EDGE,{"derivedFrom":[makeQuery(id+"F13.boolean.opBoolean","COPY",FACE,{"disambiguationData":[TD([subQ6])],"derivedFrom":makeQuery(id+"F13.opExtrude","SWEPT_FACE",FACE,{"disambiguationData":[OSD([sQuery(id+"F2.wireOp",EDGE,"E4")])]})}),makeQuery(id+"F14.opExtrude","SWEPT_FACE",FACE,{"disambiguationData":[OSD([sQuery(id+"F3.wireOp",EDGE,"E5")])]})]});}
            var Q18;
            {var subQ2=sQuery(id+"F0.wireOp",EDGE,"E0");var subQ3=makeQuery(id+"F11.opRevolve","SWEPT_FACE",FACE,{"disambiguationData":[OSD([subQ2])]});Q18=makeQuery(id+"F14.boolean.opBoolean","INTERSECT",EDGE,{"derivedFrom":[makeQuery(id+"F13.boolean.opBoolean","COPY",FACE,{"disambiguationData":[TD([subQ3])],"derivedFrom":makeQuery(id+"F13.opExtrude","SWEPT_FACE",FACE,{"disambiguationData":[OSD([sQuery(id+"F2.wireOp",EDGE,"E4")])]})}),makeQuery(id+"F14.opExtrude","SWEPT_FACE",FACE,{"disambiguationData":[OSD([sQuery(id+"F3.wireOp",EDGE,"E5")])]})]});}
            var Q19;
            {var subQ0=sQuery(id+"F0.wireOp",EDGE,"E0");Q19=makeQuery(id+"F14.boolean.opBoolean","INTERSECT",EDGE,{"derivedFrom":[makeQuery(id+"F12.boolean.opBoolean","COPY",FACE,{"disambiguationData":[TD([makeQuery(id+"F11.opRevolve","SWEPT_FACE",FACE,{"disambiguationData":[OSD([subQ0])]})])],"derivedFrom":makeQuery(id+"F12.opExtrude","SWEPT_FACE",FACE,{"disambiguationData":[OSD([sQuery(id+"F1.wireOp",EDGE,"E3")])]})}),makeQuery(id+"F14.opExtrude","SWEPT_FACE",FACE,{"disambiguationData":[OSD([sQuery(id+"F3.wireOp",EDGE,"E5")])]})]});}
            var Q20;
            {var subQ0=sQuery(id+"F0.wireOp",EDGE,"E0");Q20=makeQuery(id+"F13.boolean.opBoolean","INTERSECT",EDGE,{"derivedFrom":[makeQuery(id+"F12.boolean.opBoolean","COPY",FACE,{"disambiguationData":[TD([makeQuery(id+"F11.opRevolve","SWEPT_FACE",FACE,{"disambiguationData":[OSD([subQ0])]})])],"derivedFrom":makeQuery(id+"F12.opExtrude","SWEPT_FACE",FACE,{"disambiguationData":[OSD([sQuery(id+"F1.wireOp",EDGE,"E3")])]})}),makeQuery(id+"F13.opExtrude","SWEPT_FACE",FACE,{"disambiguationData":[OSD([sQuery(id+"F2.wireOp",EDGE,"E4")])]})]});}
            var Q21;
            {var subQ0=sQuery(id+"F0.wireOp",EDGE,"E0");Q21=makeQuery(id+"F13.boolean.opBoolean","INTERSECT",EDGE,{"derivedFrom":[makeQuery(id+"F12.boolean.opBoolean","COPY",FACE,{"disambiguationData":[TD([makeQuery(id+"F9.opRevolve","SWEPT_FACE",FACE,{"disambiguationData":[OSD([subQ0])]})])],"derivedFrom":makeQuery(id+"F12.opExtrude","SWEPT_FACE",FACE,{"disambiguationData":[OSD([sQuery(id+"F1.wireOp",EDGE,"E3")])]})}),makeQuery(id+"F13.opExtrude","SWEPT_FACE",FACE,{"disambiguationData":[OSD([sQuery(id+"F2.wireOp",EDGE,"E4")])]})]});}
            var Q22;
            {var subQ0=sQuery(id+"F0.wireOp",EDGE,"E0");Q22=makeQuery(id+"F14.boolean.opBoolean","INTERSECT",EDGE,{"derivedFrom":[makeQuery(id+"F12.boolean.opBoolean","COPY",FACE,{"disambiguationData":[TD([makeQuery(id+"F8.opRevolve","SWEPT_FACE",FACE,{"disambiguationData":[OSD([subQ0])]})])],"derivedFrom":makeQuery(id+"F12.opExtrude","SWEPT_FACE",FACE,{"disambiguationData":[OSD([sQuery(id+"F1.wireOp",EDGE,"E3")])]})}),makeQuery(id+"F14.opExtrude","SWEPT_FACE",FACE,{"disambiguationData":[OSD([sQuery(id+"F3.wireOp",EDGE,"E5")])]})]});}
            var Q23;
            {var subQ0=sQuery(id+"F0.wireOp",EDGE,"E0");Q23=makeQuery(id+"F14.boolean.opBoolean","INTERSECT",EDGE,{"derivedFrom":[makeQuery(id+"F12.boolean.opBoolean","COPY",FACE,{"disambiguationData":[TD([makeQuery(id+"F10.opRevolve","SWEPT_FACE",FACE,{"disambiguationData":[OSD([subQ0])]})])],"derivedFrom":makeQuery(id+"F12.opExtrude","SWEPT_FACE",FACE,{"disambiguationData":[OSD([sQuery(id+"F1.wireOp",EDGE,"E3")])]})}),makeQuery(id+"F14.opExtrude","SWEPT_FACE",FACE,{"disambiguationData":[OSD([sQuery(id+"F3.wireOp",EDGE,"E5")])]})]});}
            fillet(context, id + "F16", {"entities" : qUnion([Q0, Q1, Q2, Q3, Q4, Q5, Q6, Q7, Q8, Q9, Q10, Q11, Q12, Q13, Q14, Q15, Q16, Q17, Q18, Q19, Q20, Q21, Q22, Q23]), "radius" : 5.08 * mm, "tangentPropagation" : true, "allowEdgeOverflow" : false});
        }
    });
